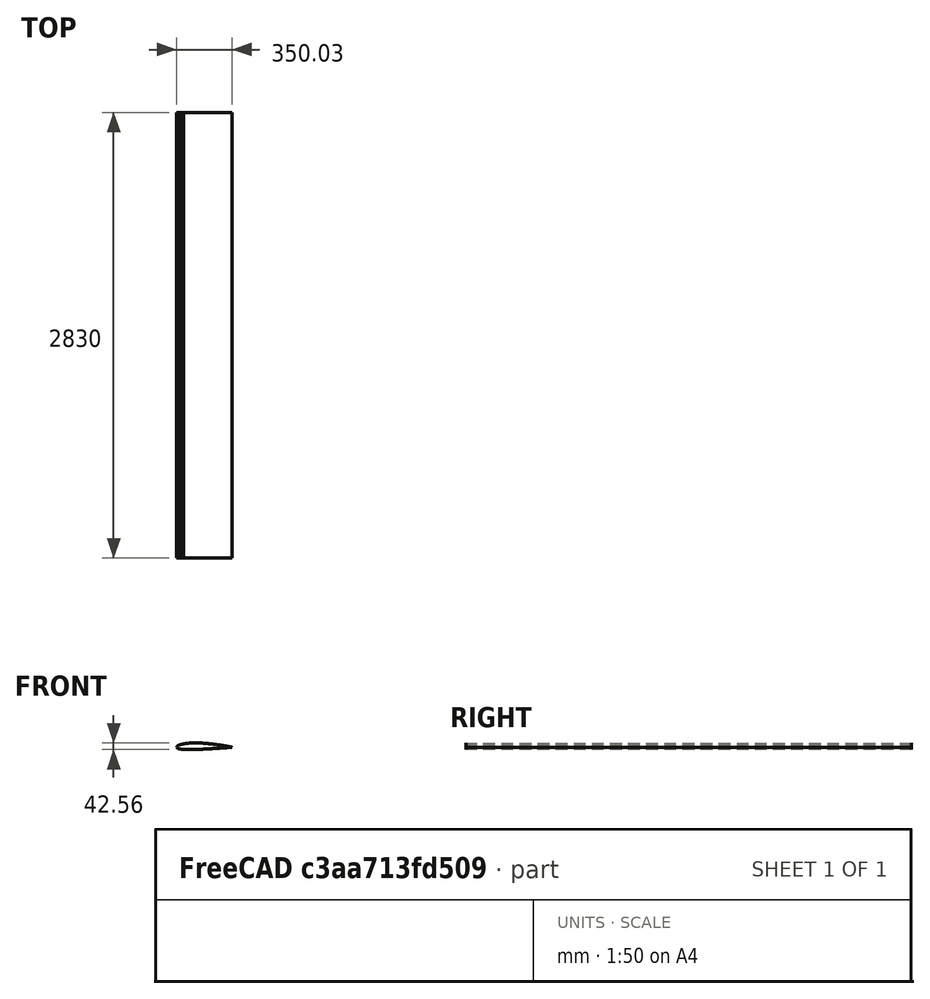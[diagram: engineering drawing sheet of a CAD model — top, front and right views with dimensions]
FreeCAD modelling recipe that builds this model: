
FCSTD DOCUMENT  (FreeCAD 1.0R39319 (Git))
Label: Airfoil-Wing
License: All rights reserved
LicenseURL: https://en.wikipedia.org/wiki/All_rights_reserved
objects: Sketcher::SketchObject×1, PartDesign::Pad×1, PartDesign::Body×1
note: 6 computed .brp shape members not serialized (recipe doc carries the construction recipe); baked Part::Feature solids carry a one-line shape summary decoded from their .brp

FEATURE [Sketcher::SketchObject] AeroFoil_1
  AirfoilChordLength = 0
  ArcFitTolerance = 1e-06
  FullyConstrained = true
  MakeInternals = false
  NumberOfPoints = 0
  Placement = pos=(0,0,0) rot=(-1,0,0;4.71239rad)
  sketch-geometry (301):
    g0: LineSegment StartX=0 StartY=0 StartZ=0 EndX=1.85273 EndY=5.11893 EndZ=0
    g1: LineSegment StartX=1.85273 StartY=5.11893 StartZ=0 EndX=4.00914 EndY=7.26084 EndZ=0
    g2: LineSegment StartX=4.00914 StartY=7.26084 StartZ=0 EndX=6.21889 EndY=8.9047 EndZ=0
    g3: LineSegment StartX=6.21889 StartY=8.9047 StartZ=0 EndX=8.45751 EndY=10.286 EndZ=0
    g4: LineSegment StartX=8.45751 StartY=10.286 StartZ=0 EndX=10.7154 EndY=11.496 EndZ=0
    g5: LineSegment StartX=10.7154 StartY=11.496 StartZ=0 EndX=12.9874 EndY=12.5816 EndZ=0
    g6: LineSegment StartX=12.9874 StartY=12.5816 StartZ=0 EndX=15.2705 EndY=13.5705 EndZ=0
    g7: LineSegment StartX=15.2705 StartY=13.5705 StartZ=0 EndX=17.5626 EndY=14.481 EndZ=0
    g8: LineSegment StartX=17.5626 StartY=14.481 StartZ=0 EndX=19.8624 EndY=15.3258 EndZ=0
    g9: LineSegment StartX=19.8624 StartY=15.3258 StartZ=0 EndX=22.1687 EndY=16.114 EndZ=0
    g10: LineSegment StartX=22.1687 StartY=16.114 StartZ=0 EndX=24.4808 EndY=16.8527 EndZ=0
    g11: LineSegment StartX=24.4808 StartY=16.8527 StartZ=0 EndX=26.7978 EndY=17.5473 EndZ=0
    g12: LineSegment StartX=26.7978 StartY=17.5473 StartZ=0 EndX=29.1194 EndY=18.2022 EndZ=0
    g13: LineSegment StartX=29.1194 StartY=18.2022 StartZ=0 EndX=31.445 EndY=18.8209 EndZ=0
    g14: LineSegment StartX=31.445 StartY=18.8209 StartZ=0 EndX=33.7742 EndY=19.4063 EndZ=0
    g15: LineSegment StartX=33.7742 StartY=19.4063 StartZ=0 EndX=36.1068 EndY=19.9609 EndZ=0
    g16: LineSegment StartX=36.1068 StartY=19.9609 StartZ=0 EndX=38.4424 EndY=20.4869 EndZ=0
    g17: LineSegment StartX=38.4424 StartY=20.4869 StartZ=0 EndX=40.7809 EndY=20.986 EndZ=0
    g18: LineSegment StartX=40.7809 StartY=20.986 StartZ=0 EndX=43.1219 EndY=21.4598 EndZ=0
    g19: LineSegment StartX=43.1219 StartY=21.4598 StartZ=0 EndX=45.4653 EndY=21.9097 EndZ=0
    g20: LineSegment StartX=45.4653 StartY=21.9097 StartZ=0 EndX=47.8109 EndY=22.3368 EndZ=0
    g21: LineSegment StartX=47.8109 StartY=22.3368 StartZ=0 EndX=50.1585 EndY=22.7423 EndZ=0
    g22: LineSegment StartX=50.1585 StartY=22.7423 StartZ=0 EndX=52.508 EndY=23.1271 EndZ=0
    g23: LineSegment StartX=52.508 StartY=23.1271 StartZ=0 EndX=54.8593 EndY=23.4922 EndZ=0
    g24: LineSegment StartX=54.8593 StartY=23.4922 StartZ=0 EndX=57.2122 EndY=23.8382 EndZ=0
    g25: LineSegment StartX=57.2122 StartY=23.8382 StartZ=0 EndX=59.5666 EndY=24.1659 EndZ=0
    g26: LineSegment StartX=59.5666 StartY=24.1659 StartZ=0 EndX=61.9224 EndY=24.4761 EndZ=0
    g27: LineSegment StartX=61.9224 StartY=24.4761 StartZ=0 EndX=64.2795 EndY=24.7691 EndZ=0
    g28: LineSegment StartX=64.2795 StartY=24.7691 StartZ=0 EndX=66.6378 EndY=25.0457 EndZ=0
    g29: LineSegment StartX=66.6378 StartY=25.0457 StartZ=0 EndX=68.9972 EndY=25.3063 EndZ=0
    g30: LineSegment StartX=68.9972 StartY=25.3063 StartZ=0 EndX=71.3576 EndY=25.5515 EndZ=0
    g31: LineSegment StartX=71.3576 StartY=25.5515 StartZ=0 EndX=73.7191 EndY=25.7816 EndZ=0
    g32: LineSegment StartX=73.7191 StartY=25.7816 StartZ=0 EndX=76.0813 EndY=25.997 EndZ=0
    g33: LineSegment StartX=76.0813 StartY=25.997 StartZ=0 EndX=78.4444 EndY=26.1983 EndZ=0
    g34: LineSegment StartX=78.4444 StartY=26.1983 StartZ=0 EndX=80.8083 EndY=26.3856 EndZ=0
    g35: LineSegment StartX=80.8083 StartY=26.3856 StartZ=0 EndX=83.1728 EndY=26.5594 EndZ=0
    g36: LineSegment StartX=83.1728 StartY=26.5594 StartZ=0 EndX=85.538 EndY=26.7199 EndZ=0
    g37: LineSegment StartX=85.538 StartY=26.7199 StartZ=0 EndX=87.9037 EndY=26.8676 EndZ=0
    g38: LineSegment StartX=87.9037 StartY=26.8676 StartZ=0 EndX=90.2699 EndY=27.0026 EndZ=0
    g39: LineSegment StartX=90.2699 StartY=27.0026 StartZ=0 EndX=92.6366 EndY=27.1253 EndZ=0
    g40: LineSegment StartX=92.6366 StartY=27.1253 StartZ=0 EndX=95.0036 EndY=27.2359 EndZ=0
    g41: LineSegment StartX=95.0036 StartY=27.2359 StartZ=0 EndX=97.3711 EndY=27.3346 EndZ=0
    g42: LineSegment StartX=97.3711 StartY=27.3346 StartZ=0 EndX=99.7388 EndY=27.4217 EndZ=0
    g43: LineSegment StartX=99.7388 StartY=27.4217 StartZ=0 EndX=102.107 EndY=27.4974 EndZ=0
    g44: LineSegment StartX=102.107 StartY=27.4974 StartZ=0 EndX=104.475 EndY=27.562 EndZ=0
    g45: LineSegment StartX=104.475 StartY=27.562 StartZ=0 EndX=106.843 EndY=27.6156 EndZ=0
    g46: LineSegment StartX=106.843 StartY=27.6156 StartZ=0 EndX=109.212 EndY=27.6584 EndZ=0
    g47: LineSegment StartX=109.212 StartY=27.6584 StartZ=0 EndX=111.581 EndY=27.6906 EndZ=0
    g48: LineSegment StartX=111.581 StartY=27.6906 StartZ=0 EndX=113.949 EndY=27.7124 EndZ=0
    g49: LineSegment StartX=113.949 StartY=27.7124 StartZ=0 EndX=116.318 EndY=27.7239 EndZ=0
    g50: LineSegment StartX=116.318 StartY=27.7239 StartZ=0 EndX=118.687 EndY=27.7254 EndZ=0
    g51: LineSegment StartX=118.687 StartY=27.7254 StartZ=0 EndX=121.055 EndY=27.717 EndZ=0
    g52: LineSegment StartX=121.055 StartY=27.717 StartZ=0 EndX=123.424 EndY=27.6989 EndZ=0
    g53: LineSegment StartX=123.424 StartY=27.6989 StartZ=0 EndX=125.793 EndY=27.6711 EndZ=0
    g54: LineSegment StartX=125.793 StartY=27.6711 StartZ=0 EndX=128.161 EndY=27.6339 EndZ=0
    g55: LineSegment StartX=128.161 StartY=27.6339 StartZ=0 EndX=130.529 EndY=27.5873 EndZ=0
    g56: LineSegment StartX=130.529 StartY=27.5873 StartZ=0 EndX=132.897 EndY=27.5316 EndZ=0
    g57: LineSegment StartX=132.897 StartY=27.5316 StartZ=0 EndX=135.265 EndY=27.4668 EndZ=0
    g58: LineSegment StartX=135.265 StartY=27.4668 StartZ=0 EndX=137.633 EndY=27.3931 EndZ=0
    g59: LineSegment StartX=137.633 StartY=27.3931 StartZ=0 EndX=140 EndY=27.3105 EndZ=0
    g60: LineSegment StartX=140 StartY=27.3105 StartZ=0 EndX=142.348 EndY=27.2204 EndZ=0
    g61: LineSegment StartX=142.348 StartY=27.2204 StartZ=0 EndX=144.696 EndY=27.1239 EndZ=0
    g62: LineSegment StartX=144.696 StartY=27.1239 StartZ=0 EndX=147.045 EndY=27.0211 EndZ=0
    g63: LineSegment StartX=147.045 StartY=27.0211 StartZ=0 EndX=149.392 EndY=26.9121 EndZ=0
    g64: LineSegment StartX=149.392 StartY=26.9121 StartZ=0 EndX=151.74 EndY=26.7971 EndZ=0
    g65: LineSegment StartX=151.74 StartY=26.7971 StartZ=0 EndX=154.088 EndY=26.6761 EndZ=0
    g66: LineSegment StartX=154.088 StartY=26.6761 StartZ=0 EndX=156.435 EndY=26.5493 EndZ=0
    g67: LineSegment StartX=156.435 StartY=26.5493 StartZ=0 EndX=158.782 EndY=26.4166 EndZ=0
    g68: LineSegment StartX=158.782 StartY=26.4166 StartZ=0 EndX=161.129 EndY=26.2783 EndZ=0
    g69: LineSegment StartX=161.129 StartY=26.2783 StartZ=0 EndX=163.476 EndY=26.1344 EndZ=0
    g70: LineSegment StartX=163.476 StartY=26.1344 StartZ=0 EndX=165.822 EndY=25.9849 EndZ=0
    g71: LineSegment StartX=165.822 StartY=25.9849 StartZ=0 EndX=168.168 EndY=25.83 EndZ=0
    g72: LineSegment StartX=168.168 StartY=25.83 StartZ=0 EndX=170.515 EndY=25.6698 EndZ=0
    g73: LineSegment StartX=170.515 StartY=25.6698 StartZ=0 EndX=172.86 EndY=25.5042 EndZ=0
    g74: LineSegment StartX=172.86 StartY=25.5042 StartZ=0 EndX=175.206 EndY=25.3335 EndZ=0
    g75: LineSegment StartX=175.206 StartY=25.3335 StartZ=0 EndX=177.551 EndY=25.1576 EndZ=0
    g76: LineSegment StartX=177.551 StartY=25.1576 StartZ=0 EndX=179.896 EndY=24.9767 EndZ=0
    g77: LineSegment StartX=179.896 StartY=24.9767 StartZ=0 EndX=182.241 EndY=24.7907 EndZ=0
    g78: LineSegment StartX=182.241 StartY=24.7907 StartZ=0 EndX=184.585 EndY=24.5998 EndZ=0
    g79: LineSegment StartX=184.585 StartY=24.5998 StartZ=0 EndX=186.93 EndY=24.404 EndZ=0
    g80: LineSegment StartX=186.93 StartY=24.404 StartZ=0 EndX=189.274 EndY=24.2034 EndZ=0
    g81: LineSegment StartX=189.274 StartY=24.2034 StartZ=0 EndX=191.617 EndY=23.998 EndZ=0
    g82: LineSegment StartX=191.617 StartY=23.998 StartZ=0 EndX=193.96 EndY=23.788 EndZ=0
    g83: LineSegment StartX=193.96 StartY=23.788 StartZ=0 EndX=196.303 EndY=23.5733 EndZ=0
    g84: LineSegment StartX=196.303 StartY=23.5733 StartZ=0 EndX=198.646 EndY=23.3539 EndZ=0
    g85: LineSegment StartX=198.646 StartY=23.3539 StartZ=0 EndX=200.989 EndY=23.1301 EndZ=0
    g86: LineSegment StartX=200.989 StartY=23.1301 StartZ=0 EndX=203.331 EndY=22.9017 EndZ=0
    g87: LineSegment StartX=203.331 StartY=22.9017 StartZ=0 EndX=205.672 EndY=22.6689 EndZ=0
    g88: LineSegment StartX=205.672 StartY=22.6689 StartZ=0 EndX=208.014 EndY=22.4317 EndZ=0
    g89: LineSegment StartX=208.014 StartY=22.4317 StartZ=0 EndX=210.355 EndY=22.1901 EndZ=0
    g90: LineSegment StartX=210.355 StartY=22.1901 StartZ=0 EndX=212.696 EndY=21.9442 EndZ=0
    g91: LineSegment StartX=212.696 StartY=21.9442 StartZ=0 EndX=215.036 EndY=21.694 EndZ=0
    g92: LineSegment StartX=215.036 StartY=21.694 StartZ=0 EndX=217.376 EndY=21.4395 EndZ=0
    g93: LineSegment StartX=217.376 StartY=21.4395 StartZ=0 EndX=219.716 EndY=21.1809 EndZ=0
    g94: LineSegment StartX=219.716 StartY=21.1809 StartZ=0 EndX=222.055 EndY=20.918 EndZ=0
    g95: LineSegment StartX=222.055 StartY=20.918 StartZ=0 EndX=224.394 EndY=20.651 EndZ=0
    g96: LineSegment StartX=224.394 StartY=20.651 StartZ=0 EndX=226.732 EndY=20.38 EndZ=0
    g97: LineSegment StartX=226.732 StartY=20.38 StartZ=0 EndX=229.071 EndY=20.1048 EndZ=0
    g98: LineSegment StartX=229.071 StartY=20.1048 StartZ=0 EndX=231.408 EndY=19.8256 EndZ=0
    g99: LineSegment StartX=231.408 StartY=19.8256 StartZ=0 EndX=233.746 EndY=19.5423 EndZ=0
    g100: LineSegment StartX=233.746 StartY=19.5423 StartZ=0 EndX=236.083 EndY=19.2551 EndZ=0
    g101: LineSegment StartX=236.083 StartY=19.2551 StartZ=0 EndX=238.42 EndY=18.9639 EndZ=0
    g102: LineSegment StartX=238.42 StartY=18.9639 StartZ=0 EndX=240.756 EndY=18.6687 EndZ=0
    g103: LineSegment StartX=240.756 StartY=18.6687 StartZ=0 EndX=243.092 EndY=18.3696 EndZ=0
    g104: LineSegment StartX=243.092 StartY=18.3696 StartZ=0 EndX=245.427 EndY=18.0666 EndZ=0
    g105: LineSegment StartX=245.427 StartY=18.0666 StartZ=0 EndX=247.762 EndY=17.7596 EndZ=0
    g106: LineSegment StartX=247.762 StartY=17.7596 StartZ=0 EndX=250.097 EndY=17.4488 EndZ=0
    g107: LineSegment StartX=250.097 StartY=17.4488 StartZ=0 EndX=252.431 EndY=17.1342 EndZ=0
    g108: LineSegment StartX=252.431 StartY=17.1342 StartZ=0 EndX=254.765 EndY=16.8157 EndZ=0
    g109: LineSegment StartX=254.765 StartY=16.8157 StartZ=0 EndX=257.098 EndY=16.4933 EndZ=0
    g110: LineSegment StartX=257.098 StartY=16.4933 StartZ=0 EndX=259.431 EndY=16.1672 EndZ=0
    g111: LineSegment StartX=259.431 StartY=16.1672 StartZ=0 EndX=261.764 EndY=15.8372 EndZ=0
    g112: LineSegment StartX=261.764 StartY=15.8372 StartZ=0 EndX=264.096 EndY=15.5034 EndZ=0
    g113: LineSegment StartX=264.096 StartY=15.5034 StartZ=0 EndX=266.427 EndY=15.1658 EndZ=0
    g114: LineSegment StartX=266.427 StartY=15.1658 StartZ=0 EndX=268.759 EndY=14.8244 EndZ=0
    g115: LineSegment StartX=268.759 StartY=14.8244 StartZ=0 EndX=271.089 EndY=14.4793 EndZ=0
    g116: LineSegment StartX=271.089 StartY=14.4793 StartZ=0 EndX=273.42 EndY=14.1303 EndZ=0
    g117: LineSegment StartX=273.42 StartY=14.1303 StartZ=0 EndX=275.749 EndY=13.7776 EndZ=0
    g118: LineSegment StartX=275.749 StartY=13.7776 StartZ=0 EndX=278.079 EndY=13.4211 EndZ=0
    g119: LineSegment StartX=278.079 StartY=13.4211 StartZ=0 EndX=280.408 EndY=13.0607 EndZ=0
    g120: LineSegment StartX=280.408 StartY=13.0607 StartZ=0 EndX=282.736 EndY=12.6967 EndZ=0
    g121: LineSegment StartX=282.736 StartY=12.6967 StartZ=0 EndX=285.064 EndY=12.3288 EndZ=0
    g122: LineSegment StartX=285.064 StartY=12.3288 StartZ=0 EndX=287.391 EndY=11.9571 EndZ=0
    g123: LineSegment StartX=287.391 StartY=11.9571 StartZ=0 EndX=289.718 EndY=11.5816 EndZ=0
    g124: LineSegment StartX=289.718 StartY=11.5816 StartZ=0 EndX=292.045 EndY=11.2024 EndZ=0
    g125: LineSegment StartX=292.045 StartY=11.2024 StartZ=0 EndX=294.371 EndY=10.8193 EndZ=0
    g126: LineSegment StartX=294.371 StartY=10.8193 StartZ=0 EndX=296.696 EndY=10.4324 EndZ=0
    g127: LineSegment StartX=296.696 StartY=10.4324 StartZ=0 EndX=299.021 EndY=10.0417 EndZ=0
    g128: LineSegment StartX=299.021 StartY=10.0417 StartZ=0 EndX=301.346 EndY=9.64708 EndZ=0
    g129: LineSegment StartX=301.346 StartY=9.64708 StartZ=0 EndX=303.669 EndY=9.24865 EndZ=0
    g130: LineSegment StartX=303.669 StartY=9.24865 StartZ=0 EndX=305.993 EndY=8.84634 EndZ=0
    g131: LineSegment StartX=305.993 StartY=8.84634 StartZ=0 EndX=308.316 EndY=8.44015 EndZ=0
    g132: LineSegment StartX=308.316 StartY=8.44015 StartZ=0 EndX=310.638 EndY=8.03006 EndZ=0
    g133: LineSegment StartX=310.638 StartY=8.03006 StartZ=0 EndX=312.96 EndY=7.61605 EndZ=0
    g134: LineSegment StartX=312.96 StartY=7.61605 StartZ=0 EndX=315.281 EndY=7.1981 EndZ=0
    g135: LineSegment StartX=315.281 StartY=7.1981 StartZ=0 EndX=317.602 EndY=6.77619 EndZ=0
    g136: LineSegment StartX=317.602 StartY=6.77619 StartZ=0 EndX=319.922 EndY=6.3503 EndZ=0
    g137: LineSegment StartX=319.922 StartY=6.3503 StartZ=0 EndX=322.241 EndY=5.92042 EndZ=0
    g138: LineSegment StartX=322.241 StartY=5.92042 StartZ=0 EndX=324.56 EndY=5.48651 EndZ=0
    g139: LineSegment StartX=324.56 StartY=5.48651 StartZ=0 EndX=326.879 EndY=5.04854 EndZ=0
    g140: LineSegment StartX=326.879 StartY=5.04854 StartZ=0 EndX=329.197 EndY=4.60651 EndZ=0
    g141: LineSegment StartX=329.197 StartY=4.60651 StartZ=0 EndX=331.514 EndY=4.16037 EndZ=0
    g142: LineSegment StartX=331.514 StartY=4.16037 StartZ=0 EndX=333.83 EndY=3.7101 EndZ=0
    g143: LineSegment StartX=333.83 StartY=3.7101 StartZ=0 EndX=336.146 EndY=3.25568 EndZ=0
    g144: LineSegment StartX=336.146 StartY=3.25568 StartZ=0 EndX=338.462 EndY=2.79706 EndZ=0
    g145: LineSegment StartX=338.462 StartY=2.79706 StartZ=0 EndX=340.777 EndY=2.33423 EndZ=0
    g146: LineSegment StartX=340.777 StartY=2.33423 StartZ=0 EndX=343.091 EndY=1.86714 EndZ=0
    g147: LineSegment StartX=343.091 StartY=1.86714 StartZ=0 EndX=345.404 EndY=1.39577 EndZ=0
    g148: LineSegment StartX=345.404 StartY=1.39577 StartZ=0 EndX=347.717 EndY=0.920075 EndZ=0
    g149: LineSegment StartX=347.717 StartY=0.920075 StartZ=0 EndX=350.029 EndY=0.440023 EndZ=0
    g150: LineSegment StartX=350.029 StartY=0.440023 StartZ=0 EndX=349.971 EndY=-0.440023 EndZ=0
    g151: LineSegment StartX=349.971 StartY=-0.440023 StartZ=0 EndX=347.616 EndY=-0.610692 EndZ=0
    g152: LineSegment StartX=347.616 StartY=-0.610692 StartZ=0 EndX=345.262 EndY=-0.780461 EndZ=0
    g153: LineSegment StartX=345.262 StartY=-0.780461 StartZ=0 EndX=342.909 EndY=-0.949365 EndZ=0
    g154: LineSegment StartX=342.909 StartY=-0.949365 StartZ=0 EndX=340.557 EndY=-1.11744 EndZ=0
    g155: LineSegment StartX=340.557 StartY=-1.11744 StartZ=0 EndX=338.205 EndY=-1.28472 EndZ=0
    g156: LineSegment StartX=338.205 StartY=-1.28472 StartZ=0 EndX=335.854 EndY=-1.45123 EndZ=0
    g157: LineSegment StartX=335.854 StartY=-1.45123 StartZ=0 EndX=333.503 EndY=-1.61702 EndZ=0
    g158: LineSegment StartX=333.503 StartY=-1.61702 StartZ=0 EndX=331.153 EndY=-1.7821 EndZ=0
    g159: LineSegment StartX=331.153 StartY=-1.7821 StartZ=0 EndX=328.803 EndY=-1.94651 EndZ=0
    g160: LineSegment StartX=328.803 StartY=-1.94651 StartZ=0 EndX=326.455 EndY=-2.11027 EndZ=0
    g161: LineSegment StartX=326.455 StartY=-2.11027 StartZ=0 EndX=324.106 EndY=-2.27342 EndZ=0
    g162: LineSegment StartX=324.106 StartY=-2.27342 StartZ=0 EndX=321.759 EndY=-2.43597 EndZ=0
    g163: LineSegment StartX=321.759 StartY=-2.43597 StartZ=0 EndX=319.411 EndY=-2.59796 EndZ=0
    g164: LineSegment StartX=319.411 StartY=-2.59796 StartZ=0 EndX=317.065 EndY=-2.7594 EndZ=0
    g165: LineSegment StartX=317.065 StartY=-2.7594 StartZ=0 EndX=314.719 EndY=-2.92032 EndZ=0
    g166: LineSegment StartX=314.719 StartY=-2.92032 StartZ=0 EndX=312.373 EndY=-3.08074 EndZ=0
    g167: LineSegment StartX=312.373 StartY=-3.08074 StartZ=0 EndX=310.029 EndY=-3.24068 EndZ=0
    g168: LineSegment StartX=310.029 StartY=-3.24068 StartZ=0 EndX=307.684 EndY=-3.40015 EndZ=0
    g169: LineSegment StartX=307.684 StartY=-3.40015 StartZ=0 EndX=305.34 EndY=-3.55918 EndZ=0
    g170: LineSegment StartX=305.34 StartY=-3.55918 StartZ=0 EndX=302.997 EndY=-3.71778 EndZ=0
    g171: LineSegment StartX=302.997 StartY=-3.71778 StartZ=0 EndX=300.654 EndY=-3.87597 EndZ=0
    g172: LineSegment StartX=300.654 StartY=-3.87597 StartZ=0 EndX=298.312 EndY=-4.03376 EndZ=0
    g173: LineSegment StartX=298.312 StartY=-4.03376 StartZ=0 EndX=295.97 EndY=-4.19116 EndZ=0
    g174: LineSegment StartX=295.97 StartY=-4.19116 StartZ=0 EndX=293.629 EndY=-4.34819 EndZ=0
    g175: LineSegment StartX=293.629 StartY=-4.34819 StartZ=0 EndX=291.289 EndY=-4.50485 EndZ=0
    g176: LineSegment StartX=291.289 StartY=-4.50485 StartZ=0 EndX=288.948 EndY=-4.66116 EndZ=0
    g177: LineSegment StartX=288.948 StartY=-4.66116 StartZ=0 EndX=286.609 EndY=-4.81712 EndZ=0
    g178: LineSegment StartX=286.609 StartY=-4.81712 StartZ=0 EndX=284.269 EndY=-4.97273 EndZ=0
    g179: LineSegment StartX=284.269 StartY=-4.97273 StartZ=0 EndX=281.931 EndY=-5.12802 EndZ=0
    g180: LineSegment StartX=281.931 StartY=-5.12802 StartZ=0 EndX=279.592 EndY=-5.28297 EndZ=0
    g181: LineSegment StartX=279.592 StartY=-5.28297 StartZ=0 EndX=277.255 EndY=-5.43759 EndZ=0
    g182: LineSegment StartX=277.255 StartY=-5.43759 StartZ=0 EndX=274.917 EndY=-5.59189 EndZ=0
    g183: LineSegment StartX=274.917 StartY=-5.59189 StartZ=0 EndX=272.58 EndY=-5.74587 EndZ=0
    g184: LineSegment StartX=272.58 StartY=-5.74587 StartZ=0 EndX=270.244 EndY=-5.89951 EndZ=0
    g185: LineSegment StartX=270.244 StartY=-5.89951 StartZ=0 EndX=267.908 EndY=-6.05283 EndZ=0
    g186: LineSegment StartX=267.908 StartY=-6.05283 StartZ=0 EndX=265.573 EndY=-6.20582 EndZ=0
    g187: LineSegment StartX=265.573 StartY=-6.20582 StartZ=0 EndX=263.238 EndY=-6.35846 EndZ=0
    g188: LineSegment StartX=263.238 StartY=-6.35846 StartZ=0 EndX=260.903 EndY=-6.51077 EndZ=0
    g189: LineSegment StartX=260.903 StartY=-6.51077 StartZ=0 EndX=258.569 EndY=-6.66273 EndZ=0
    g190: LineSegment StartX=258.569 StartY=-6.66273 StartZ=0 EndX=256.235 EndY=-6.81433 EndZ=0
    g191: LineSegment StartX=256.235 StartY=-6.81433 StartZ=0 EndX=253.902 EndY=-6.96556 EndZ=0
    g192: LineSegment StartX=253.902 StartY=-6.96556 StartZ=0 EndX=251.569 EndY=-7.11641 EndZ=0
    g193: LineSegment StartX=251.569 StartY=-7.11641 StartZ=0 EndX=249.236 EndY=-7.26687 EndZ=0
    g194: LineSegment StartX=249.236 StartY=-7.26687 StartZ=0 EndX=246.904 EndY=-7.41692 EndZ=0
    g195: LineSegment StartX=246.904 StartY=-7.41692 StartZ=0 EndX=244.573 EndY=-7.56656 EndZ=0
    g196: LineSegment StartX=244.573 StartY=-7.56656 StartZ=0 EndX=242.242 EndY=-7.71575 EndZ=0
    g197: LineSegment StartX=242.242 StartY=-7.71575 StartZ=0 EndX=239.911 EndY=-7.86449 EndZ=0
    g198: LineSegment StartX=239.911 StartY=-7.86449 StartZ=0 EndX=237.58 EndY=-8.01275 EndZ=0
    g199: LineSegment StartX=237.58 StartY=-8.01275 StartZ=0 EndX=235.25 EndY=-8.16051 EndZ=0
    g200: LineSegment StartX=235.25 StartY=-8.16051 StartZ=0 EndX=232.921 EndY=-8.30776 EndZ=0
    g201: LineSegment StartX=232.921 StartY=-8.30776 StartZ=0 EndX=230.592 EndY=-8.45446 EndZ=0
    g202: LineSegment StartX=230.592 StartY=-8.45446 StartZ=0 EndX=228.263 EndY=-8.60059 EndZ=0
    g203: LineSegment StartX=228.263 StartY=-8.60059 StartZ=0 EndX=225.934 EndY=-8.74613 EndZ=0
    g204: LineSegment StartX=225.934 StartY=-8.74613 StartZ=0 EndX=223.606 EndY=-8.89104 EndZ=0
    g205: LineSegment StartX=223.606 StartY=-8.89104 StartZ=0 EndX=221.278 EndY=-9.0353 EndZ=0
    g206: LineSegment StartX=221.278 StartY=-9.0353 StartZ=0 EndX=218.951 EndY=-9.17888 EndZ=0
    g207: LineSegment StartX=218.951 StartY=-9.17888 StartZ=0 EndX=216.624 EndY=-9.32173 EndZ=0
    g208: LineSegment StartX=216.624 StartY=-9.32173 StartZ=0 EndX=214.297 EndY=-9.46383 EndZ=0
    g209: LineSegment StartX=214.297 StartY=-9.46383 StartZ=0 EndX=211.971 EndY=-9.60514 EndZ=0
    g210: LineSegment StartX=211.971 StartY=-9.60514 StartZ=0 EndX=209.645 EndY=-9.74563 EndZ=0
    g211: LineSegment StartX=209.645 StartY=-9.74563 StartZ=0 EndX=207.32 EndY=-9.88524 EndZ=0
    g212: LineSegment StartX=207.32 StartY=-9.88524 StartZ=0 EndX=204.994 EndY=-10.024 EndZ=0
    g213: LineSegment StartX=204.994 StartY=-10.024 StartZ=0 EndX=202.669 EndY=-10.1617 EndZ=0
    g214: LineSegment StartX=202.669 StartY=-10.1617 StartZ=0 EndX=200.345 EndY=-10.2985 EndZ=0
    g215: LineSegment StartX=200.345 StartY=-10.2985 StartZ=0 EndX=198.02 EndY=-10.4342 EndZ=0
    g216: LineSegment StartX=198.02 StartY=-10.4342 StartZ=0 EndX=195.697 EndY=-10.5688 EndZ=0
    g217: LineSegment StartX=195.697 StartY=-10.5688 StartZ=0 EndX=193.373 EndY=-10.7023 EndZ=0
    g218: LineSegment StartX=193.373 StartY=-10.7023 StartZ=0 EndX=191.05 EndY=-10.8346 EndZ=0
    g219: LineSegment StartX=191.05 StartY=-10.8346 StartZ=0 EndX=188.726 EndY=-10.9656 EndZ=0
    g220: LineSegment StartX=188.726 StartY=-10.9656 StartZ=0 EndX=186.404 EndY=-11.0954 EndZ=0
    g221: LineSegment StartX=186.404 StartY=-11.0954 StartZ=0 EndX=184.081 EndY=-11.2237 EndZ=0
    g222: LineSegment StartX=184.081 StartY=-11.2237 StartZ=0 EndX=181.759 EndY=-11.3507 EndZ=0
    g223: LineSegment StartX=181.759 StartY=-11.3507 StartZ=0 EndX=179.437 EndY=-11.4762 EndZ=0
    g224: LineSegment StartX=179.437 StartY=-11.4762 StartZ=0 EndX=177.116 EndY=-11.6001 EndZ=0
    g225: LineSegment StartX=177.116 StartY=-11.6001 StartZ=0 EndX=174.794 EndY=-11.7224 EndZ=0
    g226: LineSegment StartX=174.794 StartY=-11.7224 StartZ=0 EndX=172.473 EndY=-11.843 EndZ=0
    g227: LineSegment StartX=172.473 StartY=-11.843 StartZ=0 EndX=170.152 EndY=-11.9619 EndZ=0
    g228: LineSegment StartX=170.152 StartY=-11.9619 StartZ=0 EndX=167.832 EndY=-12.0789 EndZ=0
    g229: LineSegment StartX=167.832 StartY=-12.0789 StartZ=0 EndX=165.511 EndY=-12.1941 EndZ=0
    g230: LineSegment StartX=165.511 StartY=-12.1941 StartZ=0 EndX=163.191 EndY=-12.3072 EndZ=0
    g231: LineSegment StartX=163.191 StartY=-12.3072 StartZ=0 EndX=160.871 EndY=-12.4183 EndZ=0
    g232: LineSegment StartX=160.871 StartY=-12.4183 StartZ=0 EndX=158.551 EndY=-12.5272 EndZ=0
    g233: LineSegment StartX=158.551 StartY=-12.5272 StartZ=0 EndX=156.232 EndY=-12.634 EndZ=0
    g234: LineSegment StartX=156.232 StartY=-12.634 StartZ=0 EndX=153.912 EndY=-12.7383 EndZ=0
    g235: LineSegment StartX=153.912 StartY=-12.7383 StartZ=0 EndX=151.593 EndY=-12.8403 EndZ=0
    g236: LineSegment StartX=151.593 StartY=-12.8403 StartZ=0 EndX=149.274 EndY=-12.9398 EndZ=0
    g237: LineSegment StartX=149.274 StartY=-12.9398 StartZ=0 EndX=146.955 EndY=-13.0366 EndZ=0
    g238: LineSegment StartX=146.955 StartY=-13.0366 StartZ=0 EndX=144.637 EndY=-13.1308 EndZ=0
    g239: LineSegment StartX=144.637 StartY=-13.1308 StartZ=0 EndX=142.318 EndY=-13.2221 EndZ=0
    g240: LineSegment StartX=142.318 StartY=-13.2221 StartZ=0 EndX=140 EndY=-13.3105 EndZ=0
    g241: LineSegment StartX=140 StartY=-13.3105 StartZ=0 EndX=137.701 EndY=-13.397 EndZ=0
    g242: LineSegment StartX=137.701 StartY=-13.397 StartZ=0 EndX=135.402 EndY=-13.4824 EndZ=0
    g243: LineSegment StartX=135.402 StartY=-13.4824 StartZ=0 EndX=133.103 EndY=-13.5666 EndZ=0
    g244: LineSegment StartX=133.103 StartY=-13.5666 StartZ=0 EndX=130.804 EndY=-13.6496 EndZ=0
    g245: LineSegment StartX=130.804 StartY=-13.6496 StartZ=0 EndX=128.506 EndY=-13.7311 EndZ=0
    g246: LineSegment StartX=128.506 StartY=-13.7311 StartZ=0 EndX=126.207 EndY=-13.8111 EndZ=0
    g247: LineSegment StartX=126.207 StartY=-13.8111 StartZ=0 EndX=123.909 EndY=-13.8894 EndZ=0
    g248: LineSegment StartX=123.909 StartY=-13.8894 StartZ=0 EndX=121.611 EndY=-13.9659 EndZ=0
    g249: LineSegment StartX=121.611 StartY=-13.9659 StartZ=0 EndX=119.313 EndY=-14.0404 EndZ=0
    g250: LineSegment StartX=119.313 StartY=-14.0404 StartZ=0 EndX=117.015 EndY=-14.1128 EndZ=0
    g251: LineSegment StartX=117.015 StartY=-14.1128 StartZ=0 EndX=114.717 EndY=-14.1829 EndZ=0
    g252: LineSegment StartX=114.717 StartY=-14.1829 StartZ=0 EndX=112.419 EndY=-14.2506 EndZ=0
    g253: LineSegment StartX=112.419 StartY=-14.2506 StartZ=0 EndX=110.121 EndY=-14.3156 EndZ=0
    g254: LineSegment StartX=110.121 StartY=-14.3156 StartZ=0 EndX=107.823 EndY=-14.3778 EndZ=0
    g255: LineSegment StartX=107.823 StartY=-14.3778 StartZ=0 EndX=105.525 EndY=-14.437 EndZ=0
    g256: LineSegment StartX=105.525 StartY=-14.437 StartZ=0 EndX=103.227 EndY=-14.493 EndZ=0
    g257: LineSegment StartX=103.227 StartY=-14.493 StartZ=0 EndX=100.928 EndY=-14.5456 EndZ=0
    g258: LineSegment StartX=100.928 StartY=-14.5456 StartZ=0 EndX=98.6289 EndY=-14.5946 EndZ=0
    g259: LineSegment StartX=98.6289 StartY=-14.5946 StartZ=0 EndX=96.3297 EndY=-14.6398 EndZ=0
    g260: LineSegment StartX=96.3297 StartY=-14.6398 StartZ=0 EndX=94.0301 EndY=-14.6809 EndZ=0
    g261: LineSegment StartX=94.0301 StartY=-14.6809 StartZ=0 EndX=91.7301 EndY=-14.7176 EndZ=0
    g262: LineSegment StartX=91.7301 StartY=-14.7176 StartZ=0 EndX=89.4297 EndY=-14.7498 EndZ=0
    g263: LineSegment StartX=89.4297 StartY=-14.7498 StartZ=0 EndX=87.1287 EndY=-14.7772 EndZ=0
    g264: LineSegment StartX=87.1287 StartY=-14.7772 StartZ=0 EndX=84.8272 EndY=-14.7994 EndZ=0
    g265: LineSegment StartX=84.8272 StartY=-14.7994 StartZ=0 EndX=82.525 EndY=-14.8161 EndZ=0
    g266: LineSegment StartX=82.525 StartY=-14.8161 StartZ=0 EndX=80.2222 EndY=-14.8271 EndZ=0
    g267: LineSegment StartX=80.2222 StartY=-14.8271 StartZ=0 EndX=77.9187 EndY=-14.832 EndZ=0
    g268: LineSegment StartX=77.9187 StartY=-14.832 StartZ=0 EndX=75.6143 EndY=-14.8305 EndZ=0
    g269: LineSegment StartX=75.6143 StartY=-14.8305 StartZ=0 EndX=73.309 EndY=-14.822 EndZ=0
    g270: LineSegment StartX=73.309 StartY=-14.822 StartZ=0 EndX=71.0028 EndY=-14.8063 EndZ=0
    g271: LineSegment StartX=71.0028 StartY=-14.8063 StartZ=0 EndX=68.6956 EndY=-14.7829 EndZ=0
    g272: LineSegment StartX=68.6956 StartY=-14.7829 StartZ=0 EndX=66.3872 EndY=-14.7513 EndZ=0
    g273: LineSegment StartX=66.3872 StartY=-14.7513 StartZ=0 EndX=64.0776 EndY=-14.7111 EndZ=0
    g274: LineSegment StartX=64.0776 StartY=-14.7111 StartZ=0 EndX=61.7668 EndY=-14.6615 EndZ=0
    g275: LineSegment StartX=61.7668 StartY=-14.6615 StartZ=0 EndX=59.4545 EndY=-14.6021 EndZ=0
    g276: LineSegment StartX=59.4545 StartY=-14.6021 StartZ=0 EndX=57.1407 EndY=-14.5322 EndZ=0
    g277: LineSegment StartX=57.1407 StartY=-14.5322 StartZ=0 EndX=54.8253 EndY=-14.451 EndZ=0
    g278: LineSegment StartX=54.8253 StartY=-14.451 StartZ=0 EndX=52.5082 EndY=-14.3579 EndZ=0
    g279: LineSegment StartX=52.5082 StartY=-14.3579 StartZ=0 EndX=50.1891 EndY=-14.2518 EndZ=0
    g280: LineSegment StartX=50.1891 StartY=-14.2518 StartZ=0 EndX=47.8681 EndY=-14.1319 EndZ=0
    g281: LineSegment StartX=47.8681 StartY=-14.1319 StartZ=0 EndX=45.5448 EndY=-13.997 EndZ=0
    g282: LineSegment StartX=45.5448 StartY=-13.997 StartZ=0 EndX=43.2191 EndY=-13.846 EndZ=0
    g283: LineSegment StartX=43.2191 StartY=-13.846 StartZ=0 EndX=40.8909 EndY=-13.6775 EndZ=0
    g284: LineSegment StartX=40.8909 StartY=-13.6775 StartZ=0 EndX=38.5599 EndY=-13.4898 EndZ=0
    g285: LineSegment StartX=38.5599 StartY=-13.4898 StartZ=0 EndX=36.2258 EndY=-13.2813 EndZ=0
    g286: LineSegment StartX=36.2258 StartY=-13.2813 StartZ=0 EndX=33.8884 EndY=-13.0497 EndZ=0
    g287: LineSegment StartX=33.8884 StartY=-13.0497 StartZ=0 EndX=31.5473 EndY=-12.7927 EndZ=0
    g288: LineSegment StartX=31.5473 StartY=-12.7927 StartZ=0 EndX=29.2022 EndY=-12.5073 EndZ=0
    g289: LineSegment StartX=29.2022 StartY=-12.5073 StartZ=0 EndX=26.8526 EndY=-12.1899 EndZ=0
    g290: LineSegment StartX=26.8526 StartY=-12.1899 StartZ=0 EndX=24.4979 EndY=-11.8362 EndZ=0
    g291: LineSegment StartX=24.4979 StartY=-11.8362 StartZ=0 EndX=22.1376 EndY=-11.4408 EndZ=0
    g292: LineSegment StartX=22.1376 StartY=-11.4408 StartZ=0 EndX=19.7707 EndY=-10.9966 EndZ=0
    g293: LineSegment StartX=19.7707 StartY=-10.9966 StartZ=0 EndX=17.3962 EndY=-10.4944 EndZ=0
    g294: LineSegment StartX=17.3962 StartY=-10.4944 StartZ=0 EndX=15.0126 EndY=-9.92155 EndZ=0
    g295: LineSegment StartX=15.0126 StartY=-9.92155 StartZ=0 EndX=12.618 EndY=-9.2599 EndZ=0
    g296: LineSegment StartX=12.618 StartY=-9.2599 StartZ=0 EndX=10.2092 EndY=-8.48156 EndZ=0
    g297: LineSegment StartX=10.2092 StartY=-8.48156 StartZ=0 EndX=7.78111 EndY=-7.5397 EndZ=0
    g298: LineSegment StartX=7.78111 StartY=-7.5397 StartZ=0 EndX=5.32419 EndY=-6.34306 EndZ=0
    g299: LineSegment StartX=5.32419 StartY=-6.34306 StartZ=0 EndX=2.81394 EndY=-4.65615 EndZ=0
    g300: LineSegment StartX=2.81394 StartY=-4.65615 StartZ=0 EndX=0 EndY=0 EndZ=0
  constraints (903):
    c: Coincident(g0,g1)
    c: Coincident(g1,g2)
    c: Coincident(g2,g3)
    c: Coincident(g3,g4)
    c: Coincident(g4,g5)
    c: Coincident(g5,g6)
    c: Coincident(g6,g7)
    c: Coincident(g7,g8)
    c: Coincident(g8,g9)
    c: Coincident(g9,g10)
    c: Coincident(g10,g11)
    c: Coincident(g11,g12)
    c: Coincident(g12,g13)
    c: Coincident(g13,g14)
    c: Coincident(g14,g15)
    c: Coincident(g15,g16)
    c: Coincident(g16,g17)
    c: Coincident(g17,g18)
    c: Coincident(g18,g19)
    c: Coincident(g19,g20)
    c: Coincident(g20,g21)
    c: Coincident(g21,g22)
    c: Coincident(g22,g23)
    c: Coincident(g23,g24)
    c: Coincident(g24,g25)
    c: Coincident(g25,g26)
    c: Coincident(g26,g27)
    c: Coincident(g27,g28)
    c: Coincident(g28,g29)
    c: Coincident(g29,g30)
    c: Coincident(g30,g31)
    c: Coincident(g31,g32)
    c: Coincident(g32,g33)
    c: Coincident(g33,g34)
    c: Coincident(g34,g35)
    c: Coincident(g35,g36)
    c: Coincident(g36,g37)
    c: Coincident(g37,g38)
    c: Coincident(g38,g39)
    c: Coincident(g39,g40)
    c: Coincident(g40,g41)
    c: Coincident(g41,g42)
    c: Coincident(g42,g43)
    c: Coincident(g43,g44)
    c: Coincident(g44,g45)
    c: Coincident(g45,g46)
    c: Coincident(g46,g47)
    c: Coincident(g47,g48)
    c: Coincident(g48,g49)
    c: Coincident(g49,g50)
    c: Coincident(g50,g51)
    c: Coincident(g51,g52)
    c: Coincident(g52,g53)
    c: Coincident(g53,g54)
    c: Coincident(g54,g55)
    c: Coincident(g55,g56)
    c: Coincident(g56,g57)
    c: Coincident(g57,g58)
    c: Coincident(g58,g59)
    c: Coincident(g59,g60)
    c: Coincident(g60,g61)
    c: Coincident(g61,g62)
    c: Coincident(g62,g63)
    c: Coincident(g63,g64)
    c: Coincident(g64,g65)
    c: Coincident(g65,g66)
    c: Coincident(g66,g67)
    c: Coincident(g67,g68)
    c: Coincident(g68,g69)
    c: Coincident(g69,g70)
    c: Coincident(g70,g71)
    c: Coincident(g71,g72)
    c: Coincident(g72,g73)
    c: Coincident(g73,g74)
    c: Coincident(g74,g75)
    c: Coincident(g75,g76)
    c: Coincident(g76,g77)
    c: Coincident(g77,g78)
    c: Coincident(g78,g79)
    c: Coincident(g79,g80)
    c: Coincident(g80,g81)
    c: Coincident(g81,g82)
    c: Coincident(g82,g83)
    c: Coincident(g83,g84)
    c: Coincident(g84,g85)
    c: Coincident(g85,g86)
    c: Coincident(g86,g87)
    c: Coincident(g87,g88)
    c: Coincident(g88,g89)
    c: Coincident(g89,g90)
    c: Coincident(g90,g91)
    c: Coincident(g91,g92)
    c: Coincident(g92,g93)
    c: Coincident(g93,g94)
    c: Coincident(g94,g95)
    c: Coincident(g95,g96)
    c: Coincident(g96,g97)
    c: Coincident(g97,g98)
    c: Coincident(g98,g99)
    c: Coincident(g99,g100)
    c: Coincident(g100,g101)
    c: Coincident(g101,g102)
    c: Coincident(g102,g103)
    c: Coincident(g103,g104)
    c: Coincident(g104,g105)
    c: Coincident(g105,g106)
    c: Coincident(g106,g107)
    c: Coincident(g107,g108)
    c: Coincident(g108,g109)
    c: Coincident(g109,g110)
    c: Coincident(g110,g111)
    c: Coincident(g111,g112)
    c: Coincident(g112,g113)
    c: Coincident(g113,g114)
    c: Coincident(g114,g115)
    c: Coincident(g115,g116)
    c: Coincident(g116,g117)
    c: Coincident(g117,g118)
    c: Coincident(g118,g119)
    c: Coincident(g119,g120)
    c: Coincident(g120,g121)
    c: Coincident(g121,g122)
    c: Coincident(g122,g123)
    c: Coincident(g123,g124)
    c: Coincident(g124,g125)
    c: Coincident(g125,g126)
    c: Coincident(g126,g127)
    c: Coincident(g127,g128)
    c: Coincident(g128,g129)
    c: Coincident(g129,g130)
    c: Coincident(g130,g131)
    c: Coincident(g131,g132)
    c: Coincident(g132,g133)
    c: Coincident(g133,g134)
    c: Coincident(g134,g135)
    c: Coincident(g135,g136)
    c: Coincident(g136,g137)
    c: Coincident(g137,g138)
    c: Coincident(g138,g139)
    c: Coincident(g139,g140)
    c: Coincident(g140,g141)
    c: Coincident(g141,g142)
    c: Coincident(g142,g143)
    c: Coincident(g143,g144)
    c: Coincident(g144,g145)
    c: Coincident(g145,g146)
    c: Coincident(g146,g147)
    c: Coincident(g147,g148)
    c: Coincident(g148,g149)
    c: Coincident(g149,g150)
    c: Coincident(g150,g151)
    c: Coincident(g151,g152)
    c: Coincident(g152,g153)
    c: Coincident(g153,g154)
    c: Coincident(g154,g155)
    c: Coincident(g155,g156)
    c: Coincident(g156,g157)
    c: Coincident(g157,g158)
    c: Coincident(g158,g159)
    c: Coincident(g159,g160)
    c: Coincident(g160,g161)
    c: Coincident(g161,g162)
    c: Coincident(g162,g163)
    c: Coincident(g163,g164)
    c: Coincident(g164,g165)
    c: Coincident(g165,g166)
    c: Coincident(g166,g167)
    c: Coincident(g167,g168)
    c: Coincident(g168,g169)
    c: Coincident(g169,g170)
    c: Coincident(g170,g171)
    c: Coincident(g171,g172)
    c: Coincident(g172,g173)
    c: Coincident(g173,g174)
    c: Coincident(g174,g175)
    c: Coincident(g175,g176)
    c: Coincident(g176,g177)
    c: Coincident(g177,g178)
    c: Coincident(g178,g179)
    c: Coincident(g179,g180)
    c: Coincident(g180,g181)
    c: Coincident(g181,g182)
    c: Coincident(g182,g183)
    c: Coincident(g183,g184)
    c: Coincident(g184,g185)
    c: Coincident(g185,g186)
    c: Coincident(g186,g187)
    c: Coincident(g187,g188)
    c: Coincident(g188,g189)
    c: Coincident(g189,g190)
    c: Coincident(g190,g191)
    c: Coincident(g191,g192)
    c: Coincident(g192,g193)
    c: Coincident(g193,g194)
    c: Coincident(g194,g195)
    c: Coincident(g195,g196)
    c: Coincident(g196,g197)
    c: Coincident(g197,g198)
    c: Coincident(g198,g199)
    c: Coincident(g199,g200)
    c: Coincident(g200,g201)
    c: Coincident(g201,g202)
    c: Coincident(g202,g203)
    c: Coincident(g203,g204)
    c: Coincident(g204,g205)
    c: Coincident(g205,g206)
    c: Coincident(g206,g207)
    c: Coincident(g207,g208)
    c: Coincident(g208,g209)
    c: Coincident(g209,g210)
    c: Coincident(g210,g211)
    c: Coincident(g211,g212)
    c: Coincident(g212,g213)
    c: Coincident(g213,g214)
    c: Coincident(g214,g215)
    c: Coincident(g215,g216)
    c: Coincident(g216,g217)
    c: Coincident(g217,g218)
    c: Coincident(g218,g219)
    c: Coincident(g219,g220)
    c: Coincident(g220,g221)
    c: Coincident(g221,g222)
    c: Coincident(g222,g223)
    c: Coincident(g223,g224)
    c: Coincident(g224,g225)
    c: Coincident(g225,g226)
    c: Coincident(g226,g227)
    c: Coincident(g227,g228)
    c: Coincident(g228,g229)
    c: Coincident(g229,g230)
    c: Coincident(g230,g231)
    c: Coincident(g231,g232)
    c: Coincident(g232,g233)
    c: Coincident(g233,g234)
    c: Coincident(g234,g235)
    c: Coincident(g235,g236)
    c: Coincident(g236,g237)
    c: Coincident(g237,g238)
    c: Coincident(g238,g239)
    c: Coincident(g239,g240)
    c: Coincident(g240,g241)
    c: Coincident(g241,g242)
    c: Coincident(g242,g243)
    c: Coincident(g243,g244)
    c: Coincident(g244,g245)
    c: Coincident(g245,g246)
    c: Coincident(g246,g247)
    c: Coincident(g247,g248)
    c: Coincident(g248,g249)
    c: Coincident(g249,g250)
    c: Coincident(g250,g251)
    c: Coincident(g251,g252)
    c: Coincident(g252,g253)
    c: Coincident(g253,g254)
    c: Coincident(g254,g255)
    c: Coincident(g255,g256)
    c: Coincident(g256,g257)
    c: Coincident(g257,g258)
    c: Coincident(g258,g259)
    c: Coincident(g259,g260)
    c: Coincident(g260,g261)
    c: Coincident(g261,g262)
    c: Coincident(g262,g263)
    c: Coincident(g263,g264)
    c: Coincident(g264,g265)
    c: Coincident(g265,g266)
    c: Coincident(g266,g267)
    c: Coincident(g267,g268)
    c: Coincident(g268,g269)
    c: Coincident(g269,g270)
    c: Coincident(g270,g271)
    c: Coincident(g271,g272)
    c: Coincident(g272,g273)
    c: Coincident(g273,g274)
    c: Coincident(g274,g275)
    c: Coincident(g275,g276)
    c: Coincident(g276,g277)
    c: Coincident(g277,g278)
    c: Coincident(g278,g279)
    c: Coincident(g279,g280)
    c: Coincident(g280,g281)
    c: Coincident(g281,g282)
    c: Coincident(g282,g283)
    c: Coincident(g283,g284)
    c: Coincident(g284,g285)
    c: Coincident(g285,g286)
    c: Coincident(g286,g287)
    c: Coincident(g287,g288)
    c: Coincident(g288,g289)
    c: Coincident(g289,g290)
    c: Coincident(g290,g291)
    c: Coincident(g291,g292)
    c: Coincident(g292,g293)
    c: Coincident(g293,g294)
    c: Coincident(g294,g295)
    c: Coincident(g295,g296)
    c: Coincident(g296,g297)
    c: Coincident(g297,g298)
    c: Coincident(g298,g299)
    c: Coincident(g299,g300)
    c: Coincident(g300,g0)
    c: DistanceX(g0) = 1.85273
    c: DistanceY(g0) = 5.11893
    c: DistanceX(g1) = 4.00914
    c: DistanceY(g1) = 7.26084
    c: DistanceX(g2) = 6.21889
    c: DistanceY(g2) = 8.9047
    c: DistanceX(g3) = 8.45751
    c: DistanceY(g3) = 10.286
    c: DistanceX(g4) = 10.7154
    c: DistanceY(g4) = 11.496
    c: DistanceX(g5) = 12.9874
    c: DistanceY(g5) = 12.5816
    c: DistanceX(g6) = 15.2705
    c: DistanceY(g6) = 13.5705
    c: DistanceX(g7) = 17.5626
    c: DistanceY(g7) = 14.481
    c: DistanceX(g8) = 19.8624
    c: DistanceY(g8) = 15.3258
    c: DistanceX(g9) = 22.1687
    c: DistanceY(g9) = 16.114
    c: DistanceX(g10) = 24.4808
    c: DistanceY(g10) = 16.8527
    c: DistanceX(g11) = 26.7978
    c: DistanceY(g11) = 17.5473
    c: DistanceX(g12) = 29.1194
    c: DistanceY(g12) = 18.2022
    c: DistanceX(g13) = 31.445
    c: DistanceY(g13) = 18.8209
    c: DistanceX(g14) = 33.7742
    c: DistanceY(g14) = 19.4063
    c: DistanceX(g15) = 36.1068
    c: DistanceY(g15) = 19.9609
    c: DistanceX(g16) = 38.4424
    c: DistanceY(g16) = 20.4869
    c: DistanceX(g17) = 40.7809
    c: DistanceY(g17) = 20.986
    c: DistanceX(g18) = 43.1219
    c: DistanceY(g18) = 21.4598
    c: DistanceX(g19) = 45.4653
    c: DistanceY(g19) = 21.9097
    c: DistanceX(g20) = 47.8109
    c: DistanceY(g20) = 22.3368
    c: DistanceX(g21) = 50.1585
    c: DistanceY(g21) = 22.7423
    c: DistanceX(g22) = 52.508
    c: DistanceY(g22) = 23.1271
    c: DistanceX(g23) = 54.8593
    c: DistanceY(g23) = 23.4922
    c: DistanceX(g24) = 57.2122
    c: DistanceY(g24) = 23.8382
    c: DistanceX(g25) = 59.5666
    c: DistanceY(g25) = 24.1659
    c: DistanceX(g26) = 61.9224
    c: DistanceY(g26) = 24.4761
    c: DistanceX(g27) = 64.2795
    c: DistanceY(g27) = 24.7691
    c: DistanceX(g28) = 66.6378
    c: DistanceY(g28) = 25.0457
    c: DistanceX(g29) = 68.9972
    c: DistanceY(g29) = 25.3063
    c: DistanceX(g30) = 71.3576
    c: DistanceY(g30) = 25.5515
    c: DistanceX(g31) = 73.7191
    c: DistanceY(g31) = 25.7816
    c: DistanceX(g32) = 76.0813
    c: DistanceY(g32) = 25.997
    c: DistanceX(g33) = 78.4444
    c: DistanceY(g33) = 26.1983
    c: DistanceX(g34) = 80.8083
    c: DistanceY(g34) = 26.3856
    c: DistanceX(g35) = 83.1728
    c: DistanceY(g35) = 26.5594
    c: DistanceX(g36) = 85.538
    c: DistanceY(g36) = 26.7199
    c: DistanceX(g37) = 87.9037
    c: DistanceY(g37) = 26.8676
    c: DistanceX(g38) = 90.2699
    c: DistanceY(g38) = 27.0026
    c: DistanceX(g39) = 92.6366
    c: DistanceY(g39) = 27.1253
    c: DistanceX(g40) = 95.0036
    c: DistanceY(g40) = 27.2359
    c: DistanceX(g41) = 97.3711
    c: DistanceY(g41) = 27.3346
    c: DistanceX(g42) = 99.7388
    c: DistanceY(g42) = 27.4217
    c: DistanceX(g43) = 102.107
    c: DistanceY(g43) = 27.4974
    c: DistanceX(g44) = 104.475
    c: DistanceY(g44) = 27.562
    c: DistanceX(g45) = 106.843
    c: DistanceY(g45) = 27.6156
    c: DistanceX(g46) = 109.212
    c: DistanceY(g46) = 27.6584
    c: DistanceX(g47) = 111.581
    c: DistanceY(g47) = 27.6906
    c: DistanceX(g48) = 113.949
    c: DistanceY(g48) = 27.7124
    c: DistanceX(g49) = 116.318
    c: DistanceY(g49) = 27.7239
    c: DistanceX(g50) = 118.687
    c: DistanceY(g50) = 27.7254
    c: DistanceX(g51) = 121.055
    c: DistanceY(g51) = 27.717
    c: DistanceX(g52) = 123.424
    c: DistanceY(g52) = 27.6989
    c: DistanceX(g53) = 125.793
    c: DistanceY(g53) = 27.6711
    c: DistanceX(g54) = 128.161
    c: DistanceY(g54) = 27.6339
    c: DistanceX(g55) = 130.529
    c: DistanceY(g55) = 27.5873
    c: DistanceX(g56) = 132.897
    c: DistanceY(g56) = 27.5316
    c: DistanceX(g57) = 135.265
    c: DistanceY(g57) = 27.4668
    c: DistanceX(g58) = 137.633
    c: DistanceY(g58) = 27.3931
    c: DistanceX(g59) = 140
    c: DistanceY(g59) = 27.3105
    c: DistanceX(g60) = 142.348
    c: DistanceY(g60) = 27.2204
    c: DistanceX(g61) = 144.696
    c: DistanceY(g61) = 27.1239
    c: DistanceX(g62) = 147.045
    c: DistanceY(g62) = 27.0211
    c: DistanceX(g63) = 149.392
    c: DistanceY(g63) = 26.9121
    c: DistanceX(g64) = 151.74
    c: DistanceY(g64) = 26.7971
    c: DistanceX(g65) = 154.088
    c: DistanceY(g65) = 26.6761
    c: DistanceX(g66) = 156.435
    c: DistanceY(g66) = 26.5493
    c: DistanceX(g67) = 158.782
    c: DistanceY(g67) = 26.4166
    c: DistanceX(g68) = 161.129
    c: DistanceY(g68) = 26.2783
    c: DistanceX(g69) = 163.476
    c: DistanceY(g69) = 26.1344
    c: DistanceX(g70) = 165.822
    c: DistanceY(g70) = 25.9849
    c: DistanceX(g71) = 168.168
    c: DistanceY(g71) = 25.83
    c: DistanceX(g72) = 170.515
    c: DistanceY(g72) = 25.6698
    c: DistanceX(g73) = 172.86
    c: DistanceY(g73) = 25.5042
    c: DistanceX(g74) = 175.206
    c: DistanceY(g74) = 25.3335
    c: DistanceX(g75) = 177.551
    c: DistanceY(g75) = 25.1576
    c: DistanceX(g76) = 179.896
    c: DistanceY(g76) = 24.9767
    c: DistanceX(g77) = 182.241
    c: DistanceY(g77) = 24.7907
    c: DistanceX(g78) = 184.585
    c: DistanceY(g78) = 24.5998
    c: DistanceX(g79) = 186.93
    c: DistanceY(g79) = 24.404
    c: DistanceX(g80) = 189.274
    c: DistanceY(g80) = 24.2034
    c: DistanceX(g81) = 191.617
    c: DistanceY(g81) = 23.998
    c: DistanceX(g82) = 193.96
    c: DistanceY(g82) = 23.788
    c: DistanceX(g83) = 196.303
    c: DistanceY(g83) = 23.5733
    c: DistanceX(g84) = 198.646
    c: DistanceY(g84) = 23.3539
    c: DistanceX(g85) = 200.989
    c: DistanceY(g85) = 23.1301
    c: DistanceX(g86) = 203.331
    c: DistanceY(g86) = 22.9017
    c: DistanceX(g87) = 205.672
    c: DistanceY(g87) = 22.6689
    c: DistanceX(g88) = 208.014
    c: DistanceY(g88) = 22.4317
    c: DistanceX(g89) = 210.355
    c: DistanceY(g89) = 22.1901
    c: DistanceX(g90) = 212.696
    c: DistanceY(g90) = 21.9442
    c: DistanceX(g91) = 215.036
    c: DistanceY(g91) = 21.694
    c: DistanceX(g92) = 217.376
    c: DistanceY(g92) = 21.4395
    c: DistanceX(g93) = 219.716
    c: DistanceY(g93) = 21.1809
    c: DistanceX(g94) = 222.055
    c: DistanceY(g94) = 20.918
    c: DistanceX(g95) = 224.394
    c: DistanceY(g95) = 20.651
    c: DistanceX(g96) = 226.732
    c: DistanceY(g96) = 20.38
    c: DistanceX(g97) = 229.071
    c: DistanceY(g97) = 20.1048
    c: DistanceX(g98) = 231.408
    c: DistanceY(g98) = 19.8256
    c: DistanceX(g99) = 233.746
    c: DistanceY(g99) = 19.5423
    c: DistanceX(g100) = 236.083
    c: DistanceY(g100) = 19.2551
    c: DistanceX(g101) = 238.42
    c: DistanceY(g101) = 18.9639
    c: DistanceX(g102) = 240.756
    c: DistanceY(g102) = 18.6687
    c: DistanceX(g103) = 243.092
    c: DistanceY(g103) = 18.3696
    c: DistanceX(g104) = 245.427
    c: DistanceY(g104) = 18.0666
    c: DistanceX(g105) = 247.762
    c: DistanceY(g105) = 17.7596
    c: DistanceX(g106) = 250.097
    c: DistanceY(g106) = 17.4488
    c: DistanceX(g107) = 252.431
    c: DistanceY(g107) = 17.1342
    c: DistanceX(g108) = 254.765
    c: DistanceY(g108) = 16.8157
    c: DistanceX(g109) = 257.098
    c: DistanceY(g109) = 16.4933
    c: DistanceX(g110) = 259.431
    c: DistanceY(g110) = 16.1672
    c: DistanceX(g111) = 261.764
    c: DistanceY(g111) = 15.8372
    c: DistanceX(g112) = 264.096
    c: DistanceY(g112) = 15.5034
    c: DistanceX(g113) = 266.427
    c: DistanceY(g113) = 15.1658
    c: DistanceX(g114) = 268.759
    c: DistanceY(g114) = 14.8244
    c: DistanceX(g115) = 271.089
    c: DistanceY(g115) = 14.4793
    c: DistanceX(g116) = 273.42
    c: DistanceY(g116) = 14.1303
    c: DistanceX(g117) = 275.749
    c: DistanceY(g117) = 13.7776
    c: DistanceX(g118) = 278.079
    c: DistanceY(g118) = 13.4211
    c: DistanceX(g119) = 280.408
    c: DistanceY(g119) = 13.0607
    c: DistanceX(g120) = 282.736
    c: DistanceY(g120) = 12.6967
    c: DistanceX(g121) = 285.064
    c: DistanceY(g121) = 12.3288
    c: DistanceX(g122) = 287.391
    c: DistanceY(g122) = 11.9571
    c: DistanceX(g123) = 289.718
    c: DistanceY(g123) = 11.5816
    c: DistanceX(g124) = 292.045
    c: DistanceY(g124) = 11.2024
    c: DistanceX(g125) = 294.371
    c: DistanceY(g125) = 10.8193
    c: DistanceX(g126) = 296.696
    c: DistanceY(g126) = 10.4324
    c: DistanceX(g127) = 299.021
    c: DistanceY(g127) = 10.0417
    c: DistanceX(g128) = 301.346
    c: DistanceY(g128) = 9.64708
    c: DistanceX(g129) = 303.669
    c: DistanceY(g129) = 9.24865
    c: DistanceX(g130) = 305.993
    c: DistanceY(g130) = 8.84634
    c: DistanceX(g131) = 308.316
    c: DistanceY(g131) = 8.44015
    c: DistanceX(g132) = 310.638
    c: DistanceY(g132) = 8.03006
    c: DistanceX(g133) = 312.96
    c: DistanceY(g133) = 7.61605
    c: DistanceX(g134) = 315.281
    c: DistanceY(g134) = 7.1981
    c: DistanceX(g135) = 317.602
    c: DistanceY(g135) = 6.77619
    c: DistanceX(g136) = 319.922
    c: DistanceY(g136) = 6.3503
    c: DistanceX(g137) = 322.241
    c: DistanceY(g137) = 5.92042
    c: DistanceX(g138) = 324.56
    c: DistanceY(g138) = 5.48651
    c: DistanceX(g139) = 326.879
    c: DistanceY(g139) = 5.04854
    c: DistanceX(g140) = 329.197
    c: DistanceY(g140) = 4.60651
    c: DistanceX(g141) = 331.514
    c: DistanceY(g141) = 4.16037
    c: DistanceX(g142) = 333.83
    c: DistanceY(g142) = 3.7101
    c: DistanceX(g143) = 336.146
    c: DistanceY(g143) = 3.25568
    c: DistanceX(g144) = 338.462
    c: DistanceY(g144) = 2.79706
    c: DistanceX(g145) = 340.777
    c: DistanceY(g145) = 2.33423
    c: DistanceX(g146) = 343.091
    c: DistanceY(g146) = 1.86714
    c: DistanceX(g147) = 345.404
    c: DistanceY(g147) = 1.39577
    c: DistanceX(g148) = 347.717
    c: DistanceY(g148) = 0.920075
    c: DistanceX(g149) = 350.029
    c: DistanceY(g149) = 0.440023
    c: DistanceX(g150) = 349.971
    c: DistanceY(g150) = -0.440023
    c: DistanceX(g151) = 347.616
    c: DistanceY(g151) = -0.610692
    c: DistanceX(g152) = 345.262
    c: DistanceY(g152) = -0.780461
    c: DistanceX(g153) = 342.909
    c: DistanceY(g153) = -0.949365
    c: DistanceX(g154) = 340.557
    c: DistanceY(g154) = -1.11744
    c: DistanceX(g155) = 338.205
    c: DistanceY(g155) = -1.28472
    c: DistanceX(g156) = 335.854
    c: DistanceY(g156) = -1.45123
    c: DistanceX(g157) = 333.503
    c: DistanceY(g157) = -1.61702
    c: DistanceX(g158) = 331.153
    c: DistanceY(g158) = -1.7821
    c: DistanceX(g159) = 328.803
    c: DistanceY(g159) = -1.94651
    c: DistanceX(g160) = 326.455
    c: DistanceY(g160) = -2.11027
    c: DistanceX(g161) = 324.106
    c: DistanceY(g161) = -2.27342
    c: DistanceX(g162) = 321.759
    c: DistanceY(g162) = -2.43597
    c: DistanceX(g163) = 319.411
    c: DistanceY(g163) = -2.59796
    c: DistanceX(g164) = 317.065
    c: DistanceY(g164) = -2.7594
    c: DistanceX(g165) = 314.719
    c: DistanceY(g165) = -2.92032
    c: DistanceX(g166) = 312.373
    c: DistanceY(g166) = -3.08074
    c: DistanceX(g167) = 310.029
    c: DistanceY(g167) = -3.24068
    c: DistanceX(g168) = 307.684
    c: DistanceY(g168) = -3.40015
    c: DistanceX(g169) = 305.34
    c: DistanceY(g169) = -3.55918
    c: DistanceX(g170) = 302.997
    c: DistanceY(g170) = -3.71778
    c: DistanceX(g171) = 300.654
    c: DistanceY(g171) = -3.87597
    c: DistanceX(g172) = 298.312
    c: DistanceY(g172) = -4.03376
    c: DistanceX(g173) = 295.97
    c: DistanceY(g173) = -4.19116
    c: DistanceX(g174) = 293.629
    c: DistanceY(g174) = -4.34819
    c: DistanceX(g175) = 291.289
    c: DistanceY(g175) = -4.50485
    c: DistanceX(g176) = 288.948
    c: DistanceY(g176) = -4.66116
    c: DistanceX(g177) = 286.609
    c: DistanceY(g177) = -4.81712
    c: DistanceX(g178) = 284.269
    c: DistanceY(g178) = -4.97273
    c: DistanceX(g179) = 281.931
    c: DistanceY(g179) = -5.12802
    c: DistanceX(g180) = 279.592
    c: DistanceY(g180) = -5.28297
    c: DistanceX(g181) = 277.255
    c: DistanceY(g181) = -5.43759
    c: DistanceX(g182) = 274.917
    c: DistanceY(g182) = -5.59189
    c: DistanceX(g183) = 272.58
    c: DistanceY(g183) = -5.74587
    c: DistanceX(g184) = 270.244
    c: DistanceY(g184) = -5.89951
    c: DistanceX(g185) = 267.908
    c: DistanceY(g185) = -6.05283
    c: DistanceX(g186) = 265.573
    c: DistanceY(g186) = -6.20582
    c: DistanceX(g187) = 263.238
    c: DistanceY(g187) = -6.35846
    c: DistanceX(g188) = 260.903
    c: DistanceY(g188) = -6.51077
    c: DistanceX(g189) = 258.569
    c: DistanceY(g189) = -6.66273
    c: DistanceX(g190) = 256.235
    c: DistanceY(g190) = -6.81433
    c: DistanceX(g191) = 253.902
    c: DistanceY(g191) = -6.96556
    c: DistanceX(g192) = 251.569
    c: DistanceY(g192) = -7.11641
    c: DistanceX(g193) = 249.236
    c: DistanceY(g193) = -7.26687
    c: DistanceX(g194) = 246.904
    c: DistanceY(g194) = -7.41692
    c: DistanceX(g195) = 244.573
    c: DistanceY(g195) = -7.56656
    c: DistanceX(g196) = 242.242
    c: DistanceY(g196) = -7.71575
    c: DistanceX(g197) = 239.911
    c: DistanceY(g197) = -7.86449
    c: DistanceX(g198) = 237.58
    c: DistanceY(g198) = -8.01275
    c: DistanceX(g199) = 235.25
    c: DistanceY(g199) = -8.16051
    c: DistanceX(g200) = 232.921
    c: DistanceY(g200) = -8.30776
    c: DistanceX(g201) = 230.592
    c: DistanceY(g201) = -8.45446
    c: DistanceX(g202) = 228.263
    c: DistanceY(g202) = -8.60059
    c: DistanceX(g203) = 225.934
    c: DistanceY(g203) = -8.74613
    c: DistanceX(g204) = 223.606
    c: DistanceY(g204) = -8.89104
    c: DistanceX(g205) = 221.278
    c: DistanceY(g205) = -9.0353
    c: DistanceX(g206) = 218.951
    c: DistanceY(g206) = -9.17888
    c: DistanceX(g207) = 216.624
    c: DistanceY(g207) = -9.32173
    c: DistanceX(g208) = 214.297
    c: DistanceY(g208) = -9.46383
    c: DistanceX(g209) = 211.971
    c: DistanceY(g209) = -9.60514
    c: DistanceX(g210) = 209.645
    c: DistanceY(g210) = -9.74563
    c: DistanceX(g211) = 207.32
    c: DistanceY(g211) = -9.88524
    c: DistanceX(g212) = 204.994
    c: DistanceY(g212) = -10.024
    c: DistanceX(g213) = 202.669
    c: DistanceY(g213) = -10.1617
    c: DistanceX(g214) = 200.345
    c: DistanceY(g214) = -10.2985
    c: DistanceX(g215) = 198.02
    c: DistanceY(g215) = -10.4342
    c: DistanceX(g216) = 195.697
    c: DistanceY(g216) = -10.5688
    c: DistanceX(g217) = 193.373
    c: DistanceY(g217) = -10.7023
    c: DistanceX(g218) = 191.05
    c: DistanceY(g218) = -10.8346
    c: DistanceX(g219) = 188.726
    c: DistanceY(g219) = -10.9656
    c: DistanceX(g220) = 186.404
    c: DistanceY(g220) = -11.0954
    c: DistanceX(g221) = 184.081
    c: DistanceY(g221) = -11.2237
    c: DistanceX(g222) = 181.759
    c: DistanceY(g222) = -11.3507
    c: DistanceX(g223) = 179.437
    c: DistanceY(g223) = -11.4762
    c: DistanceX(g224) = 177.116
    c: DistanceY(g224) = -11.6001
    c: DistanceX(g225) = 174.794
    c: DistanceY(g225) = -11.7224
    c: DistanceX(g226) = 172.473
    c: DistanceY(g226) = -11.843
    c: DistanceX(g227) = 170.152
    c: DistanceY(g227) = -11.9619
    c: DistanceX(g228) = 167.832
    c: DistanceY(g228) = -12.0789
    c: DistanceX(g229) = 165.511
    c: DistanceY(g229) = -12.1941
    c: DistanceX(g230) = 163.191
    c: DistanceY(g230) = -12.3072
    c: DistanceX(g231) = 160.871
    c: DistanceY(g231) = -12.4183
    c: DistanceX(g232) = 158.551
    c: DistanceY(g232) = -12.5272
    c: DistanceX(g233) = 156.232
    c: DistanceY(g233) = -12.634
    c: DistanceX(g234) = 153.912
    c: DistanceY(g234) = -12.7383
    c: DistanceX(g235) = 151.593
    c: DistanceY(g235) = -12.8403
    c: DistanceX(g236) = 149.274
    c: DistanceY(g236) = -12.9398
    c: DistanceX(g237) = 146.955
    c: DistanceY(g237) = -13.0366
    c: DistanceX(g238) = 144.637
    c: DistanceY(g238) = -13.1308
    c: DistanceX(g239) = 142.318
    c: DistanceY(g239) = -13.2221
    c: DistanceX(g240) = 140
    c: DistanceY(g240) = -13.3105
    c: DistanceX(g241) = 137.701
    c: DistanceY(g241) = -13.397
    c: DistanceX(g242) = 135.402
    c: DistanceY(g242) = -13.4824
    c: DistanceX(g243) = 133.103
    c: DistanceY(g243) = -13.5666
    c: DistanceX(g244) = 130.804
    c: DistanceY(g244) = -13.6496
    c: DistanceX(g245) = 128.506
    c: DistanceY(g245) = -13.7311
    c: DistanceX(g246) = 126.207
    c: DistanceY(g246) = -13.8111
    c: DistanceX(g247) = 123.909
    c: DistanceY(g247) = -13.8894
    c: DistanceX(g248) = 121.611
    c: DistanceY(g248) = -13.9659
    c: DistanceX(g249) = 119.313
    c: DistanceY(g249) = -14.0404
    c: DistanceX(g250) = 117.015
    c: DistanceY(g250) = -14.1128
    c: DistanceX(g251) = 114.717
    c: DistanceY(g251) = -14.1829
    c: DistanceX(g252) = 112.419
    c: DistanceY(g252) = -14.2506
    c: DistanceX(g253) = 110.121
    c: DistanceY(g253) = -14.3156
    c: DistanceX(g254) = 107.823
    c: DistanceY(g254) = -14.3778
    c: DistanceX(g255) = 105.525
    c: DistanceY(g255) = -14.437
    c: DistanceX(g256) = 103.227
    c: DistanceY(g256) = -14.493
    c: DistanceX(g257) = 100.928
    c: DistanceY(g257) = -14.5456
    c: DistanceX(g258) = 98.6289
    c: DistanceY(g258) = -14.5946
    c: DistanceX(g259) = 96.3297
    c: DistanceY(g259) = -14.6398
    c: DistanceX(g260) = 94.0301
    c: DistanceY(g260) = -14.6809
    c: DistanceX(g261) = 91.7301
    c: DistanceY(g261) = -14.7176
    c: DistanceX(g262) = 89.4297
    c: DistanceY(g262) = -14.7498
    c: DistanceX(g263) = 87.1287
    c: DistanceY(g263) = -14.7772
    c: DistanceX(g264) = 84.8272
    c: DistanceY(g264) = -14.7994
    c: DistanceX(g265) = 82.525
    c: DistanceY(g265) = -14.8161
    c: DistanceX(g266) = 80.2222
    c: DistanceY(g266) = -14.8271
    c: DistanceX(g267) = 77.9187
    c: DistanceY(g267) = -14.832
    c: DistanceX(g268) = 75.6143
    c: DistanceY(g268) = -14.8305
    c: DistanceX(g269) = 73.309
    c: DistanceY(g269) = -14.822
    c: DistanceX(g270) = 71.0028
    c: DistanceY(g270) = -14.8063
    c: DistanceX(g271) = 68.6956
    c: DistanceY(g271) = -14.7829
    c: DistanceX(g272) = 66.3872
    c: DistanceY(g272) = -14.7513
    c: DistanceX(g273) = 64.0776
    c: DistanceY(g273) = -14.7111
    c: DistanceX(g274) = 61.7668
    c: DistanceY(g274) = -14.6615
    c: DistanceX(g275) = 59.4545
    c: DistanceY(g275) = -14.6021
    c: DistanceX(g276) = 57.1407
    c: DistanceY(g276) = -14.5322
    c: DistanceX(g277) = 54.8253
    c: DistanceY(g277) = -14.451
    c: DistanceX(g278) = 52.5082
    c: DistanceY(g278) = -14.3579
    c: DistanceX(g279) = 50.1891
    c: DistanceY(g279) = -14.2518
    c: DistanceX(g280) = 47.8681
    c: DistanceY(g280) = -14.1319
    c: DistanceX(g281) = 45.5448
    c: DistanceY(g281) = -13.997
    c: DistanceX(g282) = 43.2191
    c: DistanceY(g282) = -13.846
    c: DistanceX(g283) = 40.8909
    c: DistanceY(g283) = -13.6775
    c: DistanceX(g284) = 38.5599
    c: DistanceY(g284) = -13.4898
    c: DistanceX(g285) = 36.2258
    c: DistanceY(g285) = -13.2813
    c: DistanceX(g286) = 33.8884
    c: DistanceY(g286) = -13.0497
    c: DistanceX(g287) = 31.5473
    c: DistanceY(g287) = -12.7927
    c: DistanceX(g288) = 29.2022
    c: DistanceY(g288) = -12.5073
    c: DistanceX(g289) = 26.8526
    c: DistanceY(g289) = -12.1899
    c: DistanceX(g290) = 24.4979
    c: DistanceY(g290) = -11.8362
    c: DistanceX(g291) = 22.1376
    c: DistanceY(g291) = -11.4408
    c: DistanceX(g292) = 19.7707
    c: DistanceY(g292) = -10.9966
    c: DistanceX(g293) = 17.3962
    c: DistanceY(g293) = -10.4944
    c: DistanceX(g294) = 15.0126
    c: DistanceY(g294) = -9.92155
    c: DistanceX(g295) = 12.618
    c: DistanceY(g295) = -9.2599
    c: DistanceX(g296) = 10.2092
    c: DistanceY(g296) = -8.48156
    c: DistanceX(g297) = 7.78111
    c: DistanceY(g297) = -7.5397
    c: DistanceX(g298) = 5.32419
    c: DistanceY(g298) = -6.34306
    c: DistanceX(g299) = 2.81394
    c: DistanceY(g299) = -4.65615
    c: DistanceX(g0) = 0
    c: DistanceY(g0) = 0
FEATURE [PartDesign::Pad] Pad
  Direction = (0,-1,0)
  Length = 2830
  Length2 = 10
  Midplane = true
  Placement = pos=(0,0,0) rot=(-1,0,0;4.71239rad)
  Profile = -> AeroFoil_1
  ReferenceAxis = -> AeroFoil_1 [N_Axis]
  Refine = true
  Suppressed = false
  Type = 0
FEATURE [PartDesign::Body] Body
  AllowCompound = false
  Group = -> [AeroFoil_1,Pad]
  Origin = -> Origin
  Tip = -> Pad
